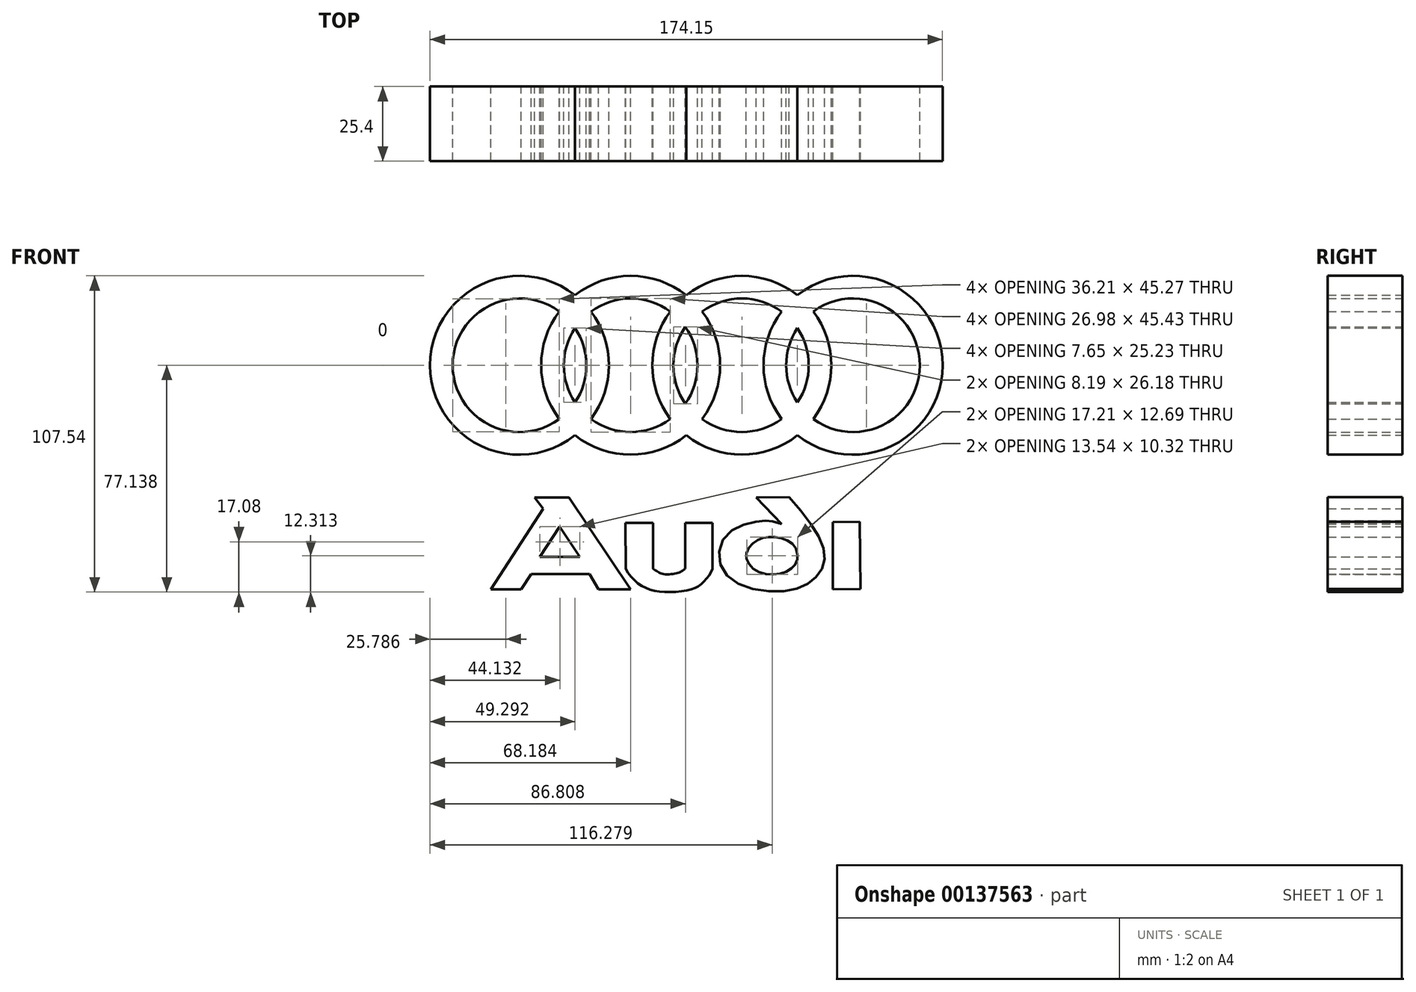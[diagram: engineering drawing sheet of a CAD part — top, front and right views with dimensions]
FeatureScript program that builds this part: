
annotation { "Feature Type Name" : "Feature", "Feature Type Description" : "" }
export const myFeature = defineFeature(function(context is Context, id is Id, definition is map)
    precondition{}
    {
        {
            var Q0;
            Q0=qCreatedBy(makeId("Front.planeOp"),FACE);
            var sketch = newSketch(context, id + "F0", { "sketchPlane" : qUnion([Q0])});
            skLineSegment(sketch, "E0", {"start": v(0, 114.35) * mm, "end": v(0, -93.25) * mm, "construction": true});
            skLineSegment(sketch, "E1", {"start": v(-133.77, 0) * mm, "end": v(38.92, 0) * mm, "construction": true});
            skArc(sketch, "E2", {"start": v(-42.86, 41.44) * mm, "mid": v(-79.07, 23.16) * mm, "end": v(-42.86, 4.88) * mm});
            skArc(sketch, "E3.1.0.0", {"start": v(-37.46, 35.77) * mm, "mid": v(-41.28, 23.16) * mm, "end": v(-37.46, 10.54) * mm});
            skArc(sketch, "E3.3.0.0", {"start": v(38.1, 35.77) * mm, "mid": v(34.28, 23.16) * mm, "end": v(38.1, 10.54) * mm});
            skLineSegment(sketch, "E3.direction1", {"start": v(-56.35, 23.16) * mm, "end": v(-18.57, 23.16) * mm, "construction": true});
            skArc(sketch, "E4", {"start": v(-37.46, 46.98) * mm, "mid": v(-86.75, 22.64) * mm, "end": v(-36.65, 0) * mm});
            skArc(sketch, "E5.1.0.0", {"start": v(-42.86, 41.44) * mm, "mid": v(-48.97, 23.16) * mm, "end": v(-42.86, 4.88) * mm});
            skArc(sketch, "E5.2.0.0", {"start": v(-5.08, 41.44) * mm, "mid": v(-11.19, 23.16) * mm, "end": v(-5.08, 4.88) * mm});
            skArc(sketch, "E5.3.0.0", {"start": v(32.7, 41.44) * mm, "mid": v(26.6, 23.16) * mm, "end": v(32.7, 4.88) * mm});
            skArc(sketch, "E6.trimOffspring", {"start": v(-5.08, 41.44) * mm, "mid": v(-18.57, 45.88) * mm, "end": v(-32.05, 41.44) * mm});
            skArc(sketch, "E7.trimOffspring", {"start": v(0.33, 46.98) * mm, "mid": v(-18.57, 53.56) * mm, "end": v(-37.46, 46.98) * mm});
            skArc(sketch, "E8.trimOffspring", {"start": v(38.1, 46.98) * mm, "mid": v(19, 53.56) * mm, "end": v(0, 46.72) * mm});
            skArc(sketch, "E9.trimOffspring", {"start": v(32.7, 41.44) * mm, "mid": v(19.22, 45.88) * mm, "end": v(5.73, 41.44) * mm});
            skArc(sketch, "E10.trimOffspring", {"start": v(38.1, 10.54) * mm, "mid": v(41.93, 23.16) * mm, "end": v(38.1, 35.77) * mm});
            skArc(sketch, "E11.trimOffspring", {"start": v(43.51, 4.88) * mm, "mid": v(79.72, 23.16) * mm, "end": v(43.51, 41.44) * mm});
            skLineSegment(sketch, "E12.trimOffspring", {"start": v(76.7, 0) * mm, "end": v(177.88, 0) * mm, "construction": true});
            skArc(sketch, "E13.trimOffspring", {"start": v(37.3, 0) * mm, "mid": v(87.4, 22.64) * mm, "end": v(38.1, 46.98) * mm});
            skArc(sketch, "E14.trimOffspring", {"start": v(43.51, 4.88) * mm, "mid": v(49.62, 23.16) * mm, "end": v(43.51, 41.44) * mm});
            skArc(sketch, "E15.trimOffspring", {"start": v(-0.48, 0) * mm, "mid": v(19.22, -7.25) * mm, "end": v(38.92, 0) * mm});
            skArc(sketch, "E16.trimOffspring", {"start": v(0, 10.07) * mm, "mid": v(4.15, 23.16) * mm, "end": v(0, 36.25) * mm});
            skArc(sketch, "E17.trimOffspring", {"start": v(5.73, 4.88) * mm, "mid": v(19.22, 0.44) * mm, "end": v(32.7, 4.88) * mm});
            skArc(sketch, "E18.trimOffspring", {"start": v(5.73, 4.88) * mm, "mid": v(11.84, 23.16) * mm, "end": v(5.73, 41.44) * mm});
            skArc(sketch, "E19.trimOffspring", {"start": v(-32.05, 4.88) * mm, "mid": v(-25.95, 23.16) * mm, "end": v(-32.05, 41.44) * mm});
            skArc(sketch, "E20.trimOffspring", {"start": v(-32.05, 4.88) * mm, "mid": v(-18.57, 0.44) * mm, "end": v(-5.08, 4.88) * mm});
            skArc(sketch, "E21.trimOffspring", {"start": v(-37.46, 10.54) * mm, "mid": v(-33.63, 23.16) * mm, "end": v(-37.46, 35.77) * mm});
            skArc(sketch, "E22.trimOffspring", {"start": v(-38.27, 0) * mm, "mid": v(-18.57, -7.25) * mm, "end": v(1.13, 0) * mm});
            skLineSegment(sketch, "E23", {"start": v(-66.02, -53.03) * mm, "end": v(-48.24, -25.6) * mm});
            skLineSegment(sketch, "E24", {"start": v(-48.24, -25.6) * mm, "end": v(-51.16, -21.78) * mm});
            skLineSegment(sketch, "E25", {"start": v(-51.16, -21.78) * mm, "end": v(-39.55, -21.78) * mm});
            skLineSegment(sketch, "E26", {"start": v(-39.55, -21.78) * mm, "end": v(-18.59, -53.03) * mm});
            skLineSegment(sketch, "E27", {"start": v(-18.59, -53.03) * mm, "end": v(-29.5, -53.03) * mm});
            skLineSegment(sketch, "E28", {"start": v(-29.5, -53.03) * mm, "end": v(-32.5, -47.82) * mm});
            skLineSegment(sketch, "E29", {"start": v(-32.5, -47.82) * mm, "end": v(-52.39, -47.82) * mm});
            skLineSegment(sketch, "E30", {"start": v(-52.39, -47.82) * mm, "end": v(-55.77, -53.03) * mm});
            skLineSegment(sketch, "E31", {"start": v(-55.77, -53.03) * mm, "end": v(-66.02, -53.03) * mm});
            skLineSegment(sketch, "E32", {"start": v(-49.4, -42.06) * mm, "end": v(-35.85, -42.06) * mm});
            skLineSegment(sketch, "E33", {"start": v(-35.85, -42.06) * mm, "end": v(-42.77, -31.74) * mm});
            skLineSegment(sketch, "E34", {"start": v(-42.77, -31.74) * mm, "end": v(-49.4, -42.06) * mm});
            skLineSegment(sketch, "E35", {"start": v(-20.38, -30.44) * mm, "end": v(-10.91, -30.44) * mm});
            skLineSegment(sketch, "E36", {"start": v(0, -30.44) * mm, "end": v(9.22, -30.44) * mm});
            skLineSegment(sketch, "E37", {"start": v(9.22, -30.44) * mm, "end": v(9.22, -46.02) * mm});
            skLineSegment(sketch, "E38", {"start": v(-20.26, -46.02) * mm, "end": v(-20.38, -30.44) * mm});
            skLineSegment(sketch, "E39", {"start": v(-10.91, -30.44) * mm, "end": v(-10.91, -46.02) * mm});
            skLineSegment(sketch, "E40", {"start": v(0, -30.44) * mm, "end": v(0, -46.02) * mm});
            skFitSpline(sketch, "E41", {"points": [v(-20.26, -46.02) * mm, v(-15, -51.77) * mm, v(-7.44, -53.93) * mm, v(2.27, -52.97) * mm, v(6.35, -50.45) * mm, v(9.22, -46.02) * mm], "startDerivative": vector(16.81, -33.1) * mm, "endDerivative": vector(9.24, 25.9) * mm});
            skFitSpline(sketch, "E42", {"points": [v(-10.91, -46.02) * mm, v(-7.56, -47.82) * mm, v(-2.16, -47.34) * mm, v(0, -46.02) * mm], "startDerivative": vector(8.81, -6.78) * mm, "endDerivative": vector(6.53, 5.27) * mm});
            skFitSpline(sketch, "E43", {"points": [v(30.45, -35.32) * mm, v(24.2, -36.48) * mm, v(20.7, -41.44) * mm, v(24.32, -46.9) * mm, v(33.15, -47.47) * mm, v(37.85, -43.66) * mm, v(36.9, -38.14) * mm, v(30.45, -35.32) * mm]});
            skFitSpline(sketch, "E44", {"points": [v(32.75, -30.9) * mm, v(26.62, -29.76) * mm, v(13.93, -34.6) * mm, v(13.65, -47.72) * mm, v(32.75, -53.7) * mm, v(44.58, -48.72) * mm, v(47.14, -39.74) * mm, v(35.31, -21.63) * mm], "startDerivative": vector(-92.32, 35.17) * mm, "endDerivative": vector(-91.15, 110.08) * mm});
            skLineSegment(sketch, "E45", {"start": v(32.75, -30.9) * mm, "end": v(24.05, -21.78) * mm});
            skLineSegment(sketch, "E46", {"start": v(24.05, -21.78) * mm, "end": v(35.31, -21.63) * mm});
            skLineSegment(sketch, "E47", {"start": v(50.14, -30.19) * mm, "end": v(59.26, -30.07) * mm});
            skLineSegment(sketch, "E48", {"start": v(59.26, -30.07) * mm, "end": v(59.55, -53) * mm});
            skLineSegment(sketch, "E49", {"start": v(59.55, -53) * mm, "end": v(50.14, -53.11) * mm});
            skLineSegment(sketch, "E50", {"start": v(50.14, -53.11) * mm, "end": v(50.14, -30.19) * mm});
            skArc(sketch, "E51", {"start": v(0, 10.07) * mm, "mid": v(-4.04, 23.16) * mm, "end": v(0, 36.25) * mm});
            skSolve(sketch);
        }
        {
            var Q0;
            Q0 = qSketchRegion(id + "F0", true);
            extrude(context, id + "F1", {"entities" : qUnion([Q0]), "depth" : 25.4 * mm});
        }
    });
